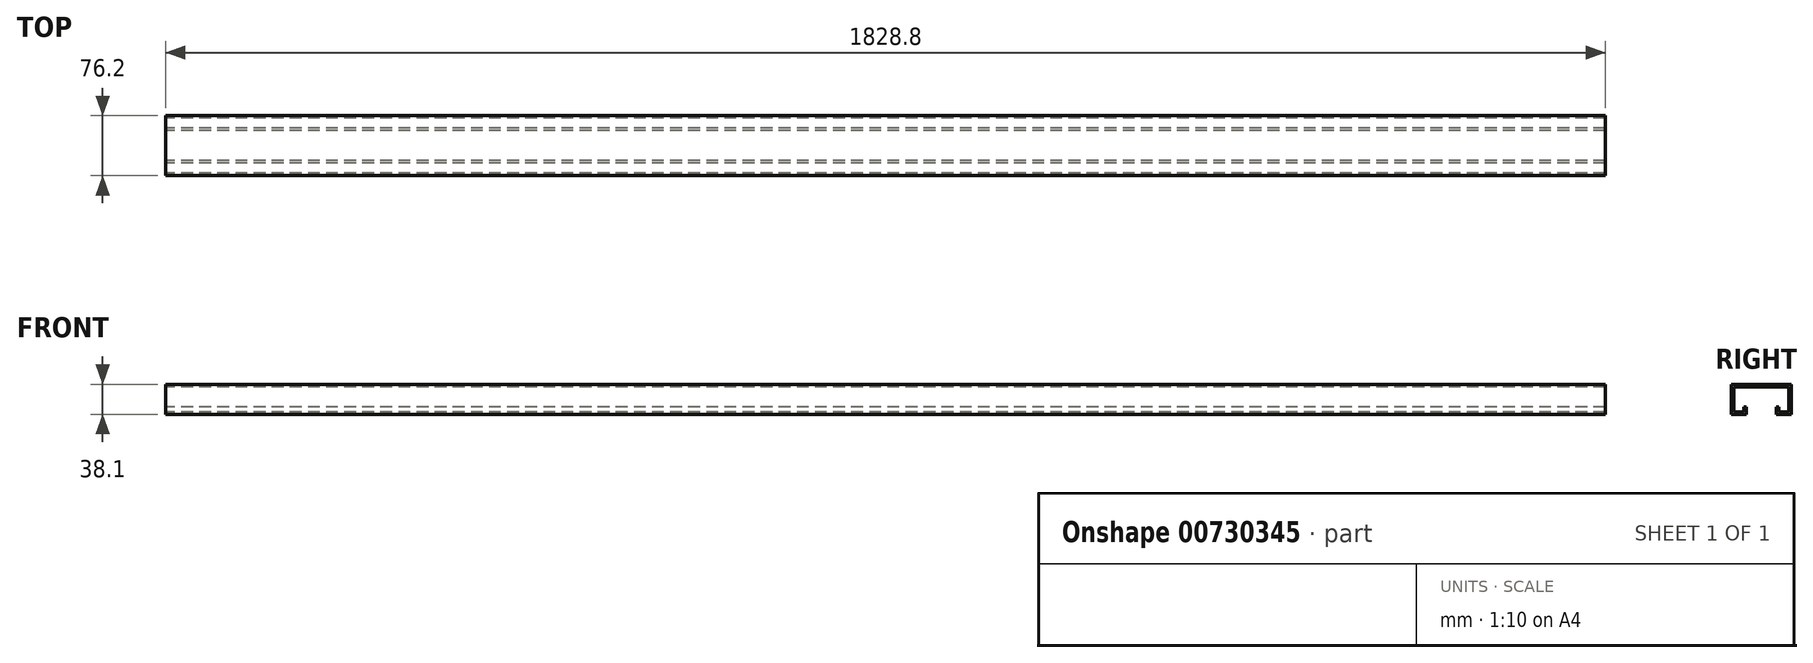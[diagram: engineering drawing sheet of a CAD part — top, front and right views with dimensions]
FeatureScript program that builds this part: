
annotation { "Feature Type Name" : "Feature", "Feature Type Description" : "" }
export const myFeature = defineFeature(function(context is Context, id is Id, definition is map)
    precondition{}
    {
        {
            var Q0;
            Q0=qCreatedBy(makeId("Right.planeOp"), FACE);
            var sketch = newSketch(context, id + "F0", { "sketchPlane" : qUnion([Q0])});
            skLineSegment(sketch, "E0", {"start": v(-19.05, 0) * mm, "end": v(-19.05, -9.53) * mm});
            skLineSegment(sketch, "E1", {"start": v(-19.05, -9.53) * mm, "end": v(-38.1, -9.53) * mm});
            skLineSegment(sketch, "E2", {"start": v(-38.1, -9.53) * mm, "end": v(-38.1, 28.58) * mm});
            skLineSegment(sketch, "E3", {"start": v(-38.1, 28.58) * mm, "end": v(0, 28.58) * mm});
            skLineSegment(sketch, "E4", {"start": v(-19.05, 0) * mm, "end": v(-22.23, 0) * mm});
            skLineSegment(sketch, "E5", {"start": v(-22.23, 0) * mm, "end": v(-22.23, -6.35) * mm});
            skLineSegment(sketch, "E6", {"start": v(-22.23, -6.35) * mm, "end": v(-34.93, -6.35) * mm});
            skLineSegment(sketch, "E7", {"start": v(-34.93, -6.35) * mm, "end": v(-34.93, 25.4) * mm});
            skLineSegment(sketch, "E8", {"start": v(-34.93, 25.4) * mm, "end": v(0, 25.4) * mm});
            skLineSegment(sketch, "E9", {"start": v(0, 28.58) * mm, "end": v(0, 25.4) * mm, "construction": true});
            skLineSegment(sketch, "E10.MirrorCS", {"start": v(34.93, 25.4) * mm, "end": v(0, 25.4) * mm});
            skLineSegment(sketch, "E11.MirrorCS", {"start": v(38.1, 28.58) * mm, "end": v(0, 28.58) * mm});
            skLineSegment(sketch, "E12.MirrorCS", {"start": v(38.1, -9.52) * mm, "end": v(38.1, 28.58) * mm});
            skLineSegment(sketch, "E13.MirrorCS", {"start": v(34.93, -6.35) * mm, "end": v(34.93, 25.4) * mm});
            skLineSegment(sketch, "E14.MirrorCS", {"start": v(19.05, 0) * mm, "end": v(19.05, -9.52) * mm});
            skLineSegment(sketch, "E15.MirrorCS", {"start": v(22.23, -6.35) * mm, "end": v(34.93, -6.35) * mm});
            skLineSegment(sketch, "E16.MirrorCS", {"start": v(19.05, -9.53) * mm, "end": v(38.1, -9.53) * mm});
            skLineSegment(sketch, "E17.MirrorCS", {"start": v(22.23, 0) * mm, "end": v(22.23, -6.35) * mm});
            skLineSegment(sketch, "E18.MirrorCS", {"start": v(19.05, 0) * mm, "end": v(22.23, 0) * mm});
            skSolve(sketch);
        }
        {
            var Q0;
            Q0 = qSketchRegion(id + "F0", true);
            extrude(context, id + "F1", {"entities" : qUnion([Q0]), "depth" : 1828.8 * mm, "offsetDistance" : 25.4 * mm});
        }
    });
